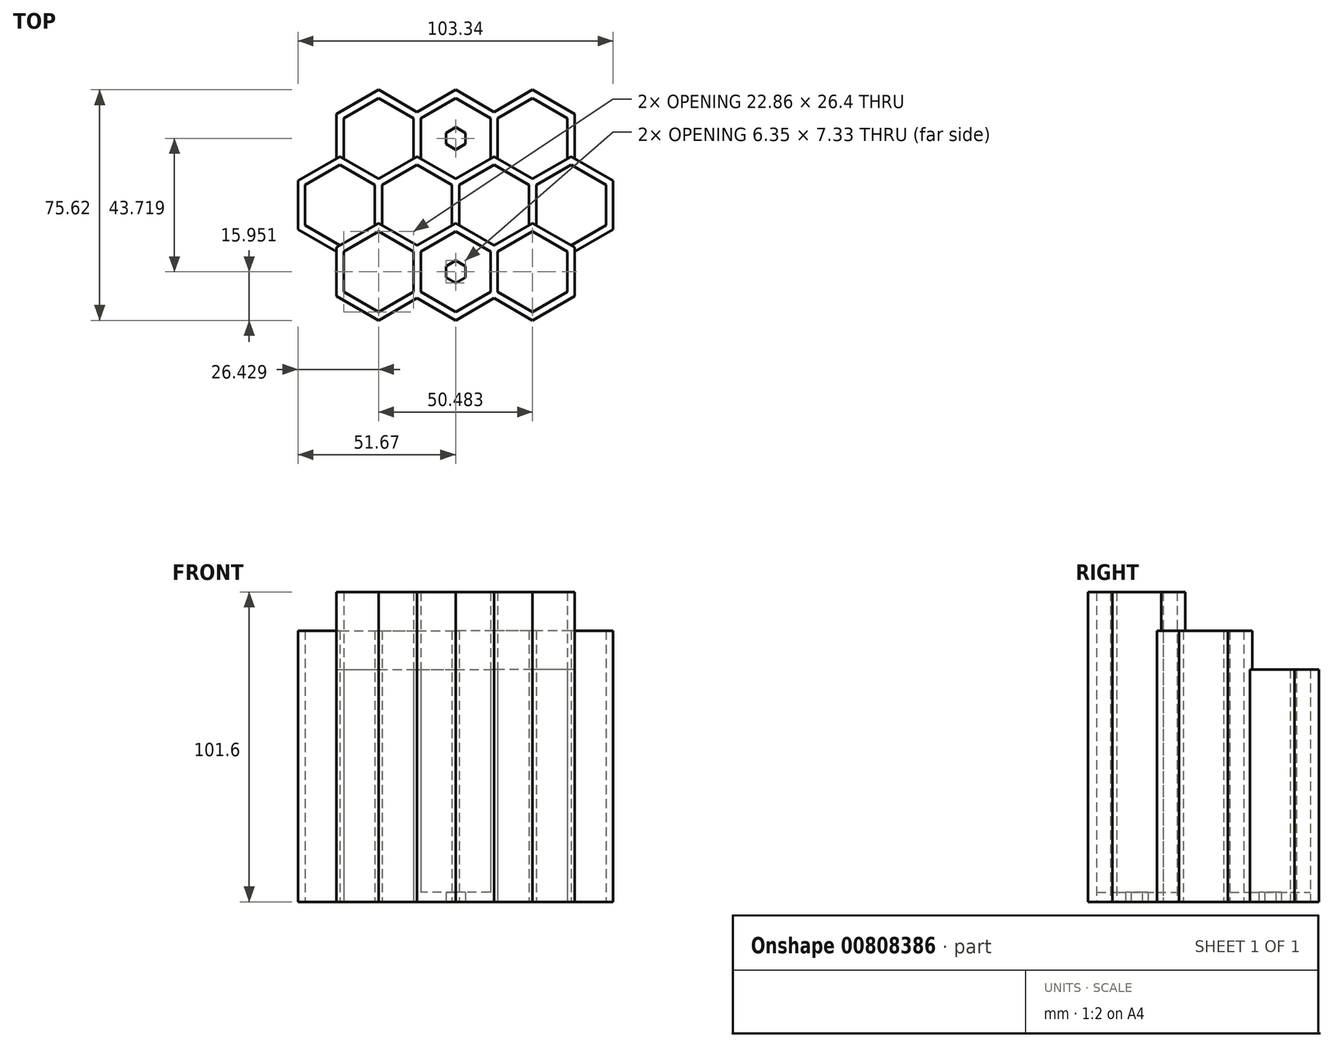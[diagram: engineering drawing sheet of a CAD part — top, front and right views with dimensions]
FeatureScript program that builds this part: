
annotation { "Feature Type Name" : "Feature", "Feature Type Description" : "" }
export const myFeature = defineFeature(function(context is Context, id is Id, definition is map)
    precondition{}
    {
        {
            var Q0;
            Q0=qCreatedBy(makeId("Top.planeOp"),FACE);
            var sketch = newSketch(context, id + "F0", { "sketchPlane" : qUnion([Q0])});
            skCircle(sketch, "E0.cCircle", {"center": v(-12.62, 0) * mm, "radius": 11.43 * mm, "construction": true});
            skLineSegment(sketch, "E0.0", {"start": v(-24.05, -6.6) * mm, "end": v(-24.05, 6.6) * mm});
            skLineSegment(sketch, "E0.1", {"start": v(-24.05, 6.6) * mm, "end": v(-12.62, 13.2) * mm});
            skLineSegment(sketch, "E0.2", {"start": v(-12.62, 13.2) * mm, "end": v(-1.2, 6.6) * mm});
            skLineSegment(sketch, "E0.3", {"start": v(-1.2, 6.6) * mm, "end": v(-1.2, -6.6) * mm});
            skLineSegment(sketch, "E0.4", {"start": v(-1.2, -6.6) * mm, "end": v(-12.62, -13.2) * mm});
            skLineSegment(sketch, "E0.5", {"start": v(-12.62, -13.2) * mm, "end": v(-24.05, -6.6) * mm});
            skPoint(sketch, "E0.0.midPoint", {"position": v(-24.05, 0) * mm});
            skCircle(sketch, "E1.cCircle", {"center": v(-37.86, 0) * mm, "radius": 11.43 * mm, "construction": true});
            skLineSegment(sketch, "E1.0", {"start": v(-49.3, -6.6) * mm, "end": v(-49.3, 6.6) * mm});
            skLineSegment(sketch, "E1.1", {"start": v(-49.3, 6.6) * mm, "end": v(-37.86, 13.2) * mm});
            skLineSegment(sketch, "E1.2", {"start": v(-37.86, 13.2) * mm, "end": v(-26.43, 6.6) * mm});
            skLineSegment(sketch, "E1.3", {"start": v(-26.43, 6.6) * mm, "end": v(-26.43, -6.6) * mm});
            skLineSegment(sketch, "E1.4", {"start": v(-26.43, -6.6) * mm, "end": v(-37.86, -13.2) * mm});
            skLineSegment(sketch, "E1.5", {"start": v(-37.86, -13.2) * mm, "end": v(-49.3, -6.6) * mm});
            skPoint(sketch, "E1.0.midPoint", {"position": v(-49.3, 0) * mm});
            skLineSegment(sketch, "E2.0", {"start": v(-37.86, 15.95) * mm, "end": v(-25.24, 8.66) * mm});
            skLineSegment(sketch, "E2.1", {"start": v(-51.67, 7.97) * mm, "end": v(-37.86, 15.95) * mm});
            skLineSegment(sketch, "E2.2", {"start": v(-51.67, -7.97) * mm, "end": v(-51.67, 7.97) * mm});
            skLineSegment(sketch, "E2.3", {"start": v(-39.05, -15.26) * mm, "end": v(-51.67, -7.97) * mm});
            skLineSegment(sketch, "E3.0", {"start": v(-12.62, 15.95) * mm, "end": v(0, 8.66) * mm});
            skLineSegment(sketch, "E3.1", {"start": v(-25.24, 8.66) * mm, "end": v(-12.62, 15.95) * mm});
            skPoint(sketch, "E4.MirrorP", {"position": v(24.05, 0) * mm});
            skLineSegment(sketch, "E5.MirrorCS", {"start": v(25.24, 8.66) * mm, "end": v(12.62, 15.95) * mm});
            skLineSegment(sketch, "E6.MirrorCS", {"start": v(39.05, -15.26) * mm, "end": v(51.67, -7.97) * mm});
            skLineSegment(sketch, "E7.MirrorCS", {"start": v(37.86, -13.2) * mm, "end": v(49.3, -6.6) * mm});
            skLineSegment(sketch, "E8.MirrorCS", {"start": v(37.86, 15.95) * mm, "end": v(25.24, 8.66) * mm});
            skLineSegment(sketch, "E9.MirrorCS", {"start": v(51.67, 7.97) * mm, "end": v(37.86, 15.95) * mm});
            skLineSegment(sketch, "E10.MirrorCS", {"start": v(24.05, 6.6) * mm, "end": v(12.62, 13.2) * mm});
            skLineSegment(sketch, "E11.MirrorCS", {"start": v(12.62, 13.2) * mm, "end": v(1.2, 6.6) * mm});
            skLineSegment(sketch, "E12.MirrorCS", {"start": v(1.2, 6.6) * mm, "end": v(1.2, -6.6) * mm});
            skLineSegment(sketch, "E13.MirrorCS", {"start": v(1.2, -6.6) * mm, "end": v(12.62, -13.2) * mm});
            skLineSegment(sketch, "E14.MirrorCS", {"start": v(12.62, -13.2) * mm, "end": v(24.05, -6.6) * mm});
            skCircle(sketch, "E15.MirrorC", {"center": v(37.86, 0) * mm, "radius": 11.43 * mm, "construction": true});
            skLineSegment(sketch, "E16.MirrorCS", {"start": v(24.05, -6.6) * mm, "end": v(24.05, 6.6) * mm});
            skPoint(sketch, "E17.MirrorP", {"position": v(49.3, 0) * mm});
            skCircle(sketch, "E18.MirrorC", {"center": v(12.62, 0) * mm, "radius": 11.43 * mm, "construction": true});
            skLineSegment(sketch, "E19.MirrorCS", {"start": v(51.67, -7.97) * mm, "end": v(51.67, 7.97) * mm});
            skLineSegment(sketch, "E20.MirrorCS", {"start": v(12.62, 15.95) * mm, "end": v(0, 8.66) * mm});
            skLineSegment(sketch, "E21.MirrorCS", {"start": v(26.43, -6.6) * mm, "end": v(37.86, -13.2) * mm});
            skLineSegment(sketch, "E22.MirrorCS", {"start": v(26.43, 6.6) * mm, "end": v(26.43, -6.6) * mm});
            skLineSegment(sketch, "E23.MirrorCS", {"start": v(37.86, 13.2) * mm, "end": v(26.43, 6.6) * mm});
            skLineSegment(sketch, "E24.MirrorCS", {"start": v(49.3, -6.6) * mm, "end": v(49.3, 6.6) * mm});
            skLineSegment(sketch, "E25.MirrorCS", {"start": v(49.3, 6.6) * mm, "end": v(37.86, 13.2) * mm});
            skLineSegment(sketch, "E26", {"start": v(-39.05, -15.26) * mm, "end": v(-37.86, -13.2) * mm});
            skLineSegment(sketch, "E27", {"start": v(-26.43, -6.6) * mm, "end": v(-24.05, -6.6) * mm});
            skLineSegment(sketch, "E28", {"start": v(-1.2, -6.6) * mm, "end": v(1.2, -6.6) * mm});
            skLineSegment(sketch, "E29", {"start": v(24.05, -6.6) * mm, "end": v(26.43, -6.6) * mm});
            skLineSegment(sketch, "E30", {"start": v(37.86, -13.2) * mm, "end": v(39.05, -15.26) * mm});
            skSolve(sketch);
        }
        {
            var Q0;
            Q0=qCreatedBy(makeId("Top.planeOp"),FACE);
            var sketch = newSketch(context, id + "F1", { "sketchPlane" : qUnion([Q0])});
            skCircle(sketch, "E31.cCircle", {"center": v(0, -21.86) * mm, "radius": 11.43 * mm, "construction": true});
            skLineSegment(sketch, "E31.0", {"start": v(-11.43, -28.46) * mm, "end": v(-11.43, -15.26) * mm});
            skLineSegment(sketch, "E31.1", {"start": v(-11.43, -15.26) * mm, "end": v(0, -8.66) * mm});
            skLineSegment(sketch, "E31.2", {"start": v(0, -8.66) * mm, "end": v(11.43, -15.26) * mm});
            skLineSegment(sketch, "E31.3", {"start": v(11.43, -15.26) * mm, "end": v(11.43, -28.46) * mm});
            skLineSegment(sketch, "E31.4", {"start": v(11.43, -28.46) * mm, "end": v(0, -35.06) * mm});
            skLineSegment(sketch, "E31.5", {"start": v(0, -35.06) * mm, "end": v(-11.43, -28.46) * mm});
            skPoint(sketch, "E31.0.midPoint", {"position": v(-11.43, -21.86) * mm});
            skLineSegment(sketch, "E32.0", {"start": v(-12.62, -13.2) * mm, "end": v(0, -5.91) * mm});
            skLineSegment(sketch, "E33.0", {"start": v(0, -5.91) * mm, "end": v(12.62, -13.2) * mm});
            skCircle(sketch, "E34.cCircle", {"center": v(-25.24, -21.86) * mm, "radius": 11.43 * mm, "construction": true});
            skLineSegment(sketch, "E34.0", {"start": v(-36.67, -28.46) * mm, "end": v(-36.67, -15.26) * mm});
            skLineSegment(sketch, "E34.1", {"start": v(-36.67, -15.26) * mm, "end": v(-25.24, -8.66) * mm});
            skLineSegment(sketch, "E34.2", {"start": v(-25.24, -8.66) * mm, "end": v(-13.81, -15.26) * mm});
            skLineSegment(sketch, "E34.3", {"start": v(-13.81, -15.26) * mm, "end": v(-13.81, -28.46) * mm});
            skLineSegment(sketch, "E34.4", {"start": v(-13.81, -28.46) * mm, "end": v(-25.24, -35.06) * mm});
            skLineSegment(sketch, "E34.5", {"start": v(-25.24, -35.06) * mm, "end": v(-36.67, -28.46) * mm});
            skPoint(sketch, "E34.0.midPoint", {"position": v(-36.67, -21.86) * mm});
            skLineSegment(sketch, "E35.0", {"start": v(-25.24, -5.91) * mm, "end": v(-12.62, -13.2) * mm});
            skLineSegment(sketch, "E35.1", {"start": v(-12.62, -30.52) * mm, "end": v(-25.24, -37.8) * mm});
            skLineSegment(sketch, "E35.2", {"start": v(-25.24, -37.8) * mm, "end": v(-39.05, -29.83) * mm});
            skLineSegment(sketch, "E35.3", {"start": v(-39.05, -29.83) * mm, "end": v(-39.05, -13.89) * mm});
            skLineSegment(sketch, "E35.4", {"start": v(-39.05, -13.89) * mm, "end": v(-25.24, -5.91) * mm});
            skLineSegment(sketch, "E36.0", {"start": v(0, -37.8) * mm, "end": v(-12.62, -30.52) * mm});
            skLineSegment(sketch, "E36.1", {"start": v(12.62, -30.52) * mm, "end": v(0, -37.8) * mm});
            skLineSegment(sketch, "E37.MirrorCS", {"start": v(13.81, -15.26) * mm, "end": v(13.81, -28.46) * mm});
            skLineSegment(sketch, "E38.MirrorCS", {"start": v(25.24, -8.66) * mm, "end": v(13.81, -15.26) * mm});
            skLineSegment(sketch, "E39.MirrorCS", {"start": v(36.67, -15.26) * mm, "end": v(25.24, -8.66) * mm});
            skLineSegment(sketch, "E40.MirrorCS", {"start": v(36.67, -28.46) * mm, "end": v(36.67, -15.26) * mm});
            skLineSegment(sketch, "E41.MirrorCS", {"start": v(25.24, -35.06) * mm, "end": v(36.67, -28.46) * mm});
            skLineSegment(sketch, "E42.MirrorCS", {"start": v(13.81, -28.46) * mm, "end": v(25.24, -35.06) * mm});
            skLineSegment(sketch, "E43.MirrorCS", {"start": v(12.62, -30.52) * mm, "end": v(25.24, -37.8) * mm});
            skLineSegment(sketch, "E44.MirrorCS", {"start": v(25.24, -37.8) * mm, "end": v(39.05, -29.83) * mm});
            skLineSegment(sketch, "E45.MirrorCS", {"start": v(39.05, -29.83) * mm, "end": v(39.05, -13.89) * mm});
            skLineSegment(sketch, "E46.MirrorCS", {"start": v(39.05, -13.89) * mm, "end": v(25.24, -5.91) * mm});
            skLineSegment(sketch, "E47.MirrorCS", {"start": v(25.24, -5.91) * mm, "end": v(12.62, -13.2) * mm});
            skSolve(sketch);
        }
        {
            var Q0;
            Q0=qCreatedBy(makeId("Top.planeOp"),FACE);
            var sketch = newSketch(context, id + "F2", { "sketchPlane" : qUnion([Q0])});
            skCircle(sketch, "E48.cCircle", {"center": v(0, 21.86) * mm, "radius": 11.43 * mm, "construction": true});
            skLineSegment(sketch, "E48.0", {"start": v(-11.43, 15.26) * mm, "end": v(-11.43, 28.46) * mm});
            skLineSegment(sketch, "E48.1", {"start": v(-11.43, 28.46) * mm, "end": v(0, 35.06) * mm});
            skLineSegment(sketch, "E48.2", {"start": v(0, 35.06) * mm, "end": v(11.43, 28.46) * mm});
            skLineSegment(sketch, "E48.3", {"start": v(11.43, 28.46) * mm, "end": v(11.43, 15.26) * mm});
            skLineSegment(sketch, "E48.4", {"start": v(11.43, 15.26) * mm, "end": v(0, 8.66) * mm});
            skLineSegment(sketch, "E48.5", {"start": v(0, 8.66) * mm, "end": v(-11.43, 15.26) * mm});
            skPoint(sketch, "E48.0.midPoint", {"position": v(-11.43, 21.86) * mm});
            skCircle(sketch, "E49.cCircle", {"center": v(-25.24, 21.86) * mm, "radius": 11.43 * mm, "construction": true});
            skLineSegment(sketch, "E49.0", {"start": v(-36.67, 15.26) * mm, "end": v(-36.67, 28.46) * mm});
            skLineSegment(sketch, "E49.1", {"start": v(-36.67, 28.46) * mm, "end": v(-25.24, 35.06) * mm});
            skLineSegment(sketch, "E49.2", {"start": v(-25.24, 35.06) * mm, "end": v(-13.81, 28.46) * mm});
            skLineSegment(sketch, "E49.3", {"start": v(-13.81, 28.46) * mm, "end": v(-13.81, 15.26) * mm});
            skLineSegment(sketch, "E49.4", {"start": v(-13.81, 15.26) * mm, "end": v(-25.24, 8.66) * mm});
            skLineSegment(sketch, "E49.5", {"start": v(-25.24, 8.66) * mm, "end": v(-36.67, 15.26) * mm});
            skPoint(sketch, "E49.0.midPoint", {"position": v(-36.67, 21.86) * mm});
            skLineSegment(sketch, "E50.0", {"start": v(-25.24, 37.8) * mm, "end": v(-12.62, 30.52) * mm});
            skLineSegment(sketch, "E50.1", {"start": v(-39.05, 29.83) * mm, "end": v(-25.24, 37.8) * mm});
            skLineSegment(sketch, "E50.2", {"start": v(-39.05, 15.26) * mm, "end": v(-39.05, 29.83) * mm});
            skLineSegment(sketch, "E51.0", {"start": v(0, 37.8) * mm, "end": v(12.62, 30.52) * mm});
            skLineSegment(sketch, "E51.1", {"start": v(-12.62, 30.52) * mm, "end": v(0, 37.8) * mm});
            skPoint(sketch, "E52.MirrorP", {"position": v(36.67, 21.86) * mm});
            skCircle(sketch, "E53.MirrorC", {"center": v(25.24, 21.86) * mm, "radius": 11.43 * mm, "construction": true});
            skLineSegment(sketch, "E54.MirrorCS", {"start": v(25.24, 8.66) * mm, "end": v(36.67, 15.26) * mm});
            skLineSegment(sketch, "E55.MirrorCS", {"start": v(36.67, 15.26) * mm, "end": v(36.67, 28.46) * mm});
            skLineSegment(sketch, "E56.MirrorCS", {"start": v(36.67, 28.46) * mm, "end": v(25.24, 35.06) * mm});
            skLineSegment(sketch, "E57.MirrorCS", {"start": v(25.24, 35.06) * mm, "end": v(13.81, 28.46) * mm});
            skLineSegment(sketch, "E58.MirrorCS", {"start": v(13.81, 28.46) * mm, "end": v(13.81, 15.26) * mm});
            skLineSegment(sketch, "E59.MirrorCS", {"start": v(13.81, 15.26) * mm, "end": v(25.24, 8.66) * mm});
            skLineSegment(sketch, "E60.MirrorCS", {"start": v(39.05, 15.26) * mm, "end": v(39.05, 29.83) * mm});
            skPoint(sketch, "E61.MirrorP", {"position": v(11.43, 21.86) * mm});
            skLineSegment(sketch, "E62.MirrorCS", {"start": v(39.05, 29.83) * mm, "end": v(25.24, 37.8) * mm});
            skLineSegment(sketch, "E63.MirrorCS", {"start": v(25.24, 37.8) * mm, "end": v(12.62, 30.52) * mm});
            skLineSegment(sketch, "E64", {"start": v(-39.05, 15.26) * mm, "end": v(-36.67, 15.26) * mm});
            skLineSegment(sketch, "E65", {"start": v(-13.81, 15.26) * mm, "end": v(-11.43, 15.26) * mm});
            skLineSegment(sketch, "E66", {"start": v(11.43, 15.26) * mm, "end": v(13.81, 15.26) * mm});
            skLineSegment(sketch, "E67", {"start": v(36.67, 15.26) * mm, "end": v(39.05, 15.26) * mm});
            skSolve(sketch);
        }
        {
            var Q0;
            Q0 = qSketchRegion(id + "F1", true);
            extrude(context, id + "F3", {"entities" : qUnion([Q0]), "depth" : 101.6 * mm, "offsetDistance" : 25.4 * mm});
        }
        {
            var Q0;
            Q0=makeQuery(id+"F0.imprint","IMPRINT",FACE,{"disambiguationData":[TD([[makeQuery(id+"F0.imprint","IMPRINT",EDGE,{"derivedFrom":sQuery(id+"F0.wireOp",EDGE,"E0.0")}),1.0]])]});
            extrude(context, id + "F4", {"entities" : qUnion([Q0]), "operationType" : NewBodyOperationType.ADD, "depth" : 88.9 * mm, "offsetDistance" : 25.4 * mm});
        }
        {
            var Q0;
            Q0=makeQuery(id+"F2.imprint","IMPRINT",FACE,{"disambiguationData":[TD([[makeQuery(id+"F2.imprint","IMPRINT",EDGE,{"derivedFrom":sQuery(id+"F2.wireOp",EDGE,"E48.0")}),1.0]])]});
            extrude(context, id + "F5", {"entities" : qUnion([Q0]), "operationType" : NewBodyOperationType.ADD, "depth" : 76.2 * mm, "offsetDistance" : 25.4 * mm});
        }
        {
            var Q0;
            Q0=qCreatedBy(makeId("Top.planeOp"),FACE);
            var sketch = newSketch(context, id + "F6", { "sketchPlane" : qUnion([Q0])});
            skCircle(sketch, "E68.cCircle", {"center": v(-12.62, 0) * mm, "radius": 11.43 * mm, "construction": true});
            skLineSegment(sketch, "E68.0", {"start": v(-24.05, -6.6) * mm, "end": v(-24.05, 6.6) * mm});
            skLineSegment(sketch, "E68.1", {"start": v(-24.05, 6.6) * mm, "end": v(-12.62, 13.2) * mm});
            skLineSegment(sketch, "E68.2", {"start": v(-12.62, 13.2) * mm, "end": v(-1.2, 6.6) * mm});
            skLineSegment(sketch, "E68.3", {"start": v(-1.2, 6.6) * mm, "end": v(-1.2, -6.6) * mm});
            skLineSegment(sketch, "E68.4", {"start": v(-1.2, -6.6) * mm, "end": v(-12.62, -13.2) * mm});
            skLineSegment(sketch, "E68.5", {"start": v(-12.62, -13.2) * mm, "end": v(-24.05, -6.6) * mm});
            skPoint(sketch, "E68.0.midPoint", {"position": v(-24.05, 0) * mm});
            skLineSegment(sketch, "E69.0", {"start": v(-49.3, -6.6) * mm, "end": v(-49.3, 6.6) * mm});
            skLineSegment(sketch, "E69.1", {"start": v(-49.3, 6.6) * mm, "end": v(-37.86, 13.2) * mm});
            skLineSegment(sketch, "E69.2", {"start": v(-37.86, 13.2) * mm, "end": v(-26.43, 6.6) * mm});
            skLineSegment(sketch, "E69.3", {"start": v(-26.43, 6.6) * mm, "end": v(-26.43, -6.6) * mm});
            skLineSegment(sketch, "E69.4", {"start": v(-26.43, -6.6) * mm, "end": v(-37.86, -13.2) * mm});
            skLineSegment(sketch, "E69.5", {"start": v(-37.86, -13.2) * mm, "end": v(-49.3, -6.6) * mm});
            skPoint(sketch, "E69.0.midPoint", {"position": v(-49.3, 0) * mm});
            skCircle(sketch, "E70.cCircle", {"center": v(-25.24, 21.86) * mm, "radius": 11.43 * mm, "construction": true});
            skLineSegment(sketch, "E70.0", {"start": v(-36.67, 15.26) * mm, "end": v(-36.67, 28.46) * mm});
            skLineSegment(sketch, "E70.1", {"start": v(-36.67, 28.46) * mm, "end": v(-25.24, 35.06) * mm});
            skLineSegment(sketch, "E70.2", {"start": v(-25.24, 35.06) * mm, "end": v(-13.81, 28.46) * mm});
            skLineSegment(sketch, "E70.3", {"start": v(-13.81, 28.46) * mm, "end": v(-13.81, 15.26) * mm});
            skLineSegment(sketch, "E70.4", {"start": v(-13.81, 15.26) * mm, "end": v(-25.24, 8.66) * mm});
            skLineSegment(sketch, "E70.5", {"start": v(-25.24, 8.66) * mm, "end": v(-36.67, 15.26) * mm});
            skPoint(sketch, "E70.0.midPoint", {"position": v(-36.67, 21.86) * mm});
            skLineSegment(sketch, "E71.MirrorCS", {"start": v(-13.81, -15.26) * mm, "end": v(-25.24, -8.66) * mm});
            skLineSegment(sketch, "E72.MirrorCS", {"start": v(-25.24, -8.66) * mm, "end": v(-36.67, -15.26) * mm});
            skLineSegment(sketch, "E73.MirrorCS", {"start": v(-36.67, -15.26) * mm, "end": v(-36.67, -28.46) * mm});
            skLineSegment(sketch, "E74.MirrorCS", {"start": v(-36.67, -28.46) * mm, "end": v(-25.24, -35.06) * mm});
            skLineSegment(sketch, "E75.MirrorCS", {"start": v(-25.24, -35.06) * mm, "end": v(-13.81, -28.46) * mm});
            skLineSegment(sketch, "E76.MirrorCS", {"start": v(-13.81, -28.46) * mm, "end": v(-13.81, -15.26) * mm});
            skLineSegment(sketch, "E77.MirrorCS", {"start": v(-1.2, -6.6) * mm, "end": v(-1.2, 6.6) * mm});
            skLineSegment(sketch, "E78.MirrorCS", {"start": v(-49.3, 6.6) * mm, "end": v(-49.3, -6.6) * mm});
            skLineSegment(sketch, "E79.MirrorCS", {"start": v(-26.43, -6.6) * mm, "end": v(-26.43, 6.6) * mm});
            skLineSegment(sketch, "E80.MirrorCS", {"start": v(-24.05, -6.6) * mm, "end": v(-12.62, -13.2) * mm});
            skLineSegment(sketch, "E81.MirrorCS", {"start": v(-36.67, 28.46) * mm, "end": v(-36.67, 15.26) * mm});
            skLineSegment(sketch, "E82.MirrorCS", {"start": v(-24.05, 6.6) * mm, "end": v(-24.05, -6.6) * mm});
            skLineSegment(sketch, "E83.MirrorCS", {"start": v(-37.86, -13.2) * mm, "end": v(-26.43, -6.6) * mm});
            skLineSegment(sketch, "E84.MirrorCS", {"start": v(-1.2, 6.6) * mm, "end": v(-12.62, 13.2) * mm});
            skPoint(sketch, "E85.MirrorP", {"position": v(-13.81, 21.86) * mm});
            skLineSegment(sketch, "E86.MirrorCS", {"start": v(-13.81, 15.26) * mm, "end": v(-13.81, 28.46) * mm});
            skLineSegment(sketch, "E87.MirrorCS", {"start": v(-49.3, -6.6) * mm, "end": v(-37.86, -13.2) * mm});
            skLineSegment(sketch, "E88.MirrorCS", {"start": v(-12.62, 13.2) * mm, "end": v(-24.05, 6.6) * mm});
            skLineSegment(sketch, "E89.MirrorCS", {"start": v(-26.43, 6.6) * mm, "end": v(-37.86, 13.2) * mm});
            skLineSegment(sketch, "E90.MirrorCS", {"start": v(-13.81, -15.26) * mm, "end": v(-13.81, -28.46) * mm});
            skLineSegment(sketch, "E91.MirrorCS", {"start": v(-37.86, 13.2) * mm, "end": v(-49.3, 6.6) * mm});
            skLineSegment(sketch, "E92.MirrorCS", {"start": v(-13.81, 28.46) * mm, "end": v(-25.24, 35.06) * mm});
            skLineSegment(sketch, "E93.MirrorCS", {"start": v(-25.24, 8.66) * mm, "end": v(-13.81, 15.26) * mm});
            skLineSegment(sketch, "E94.MirrorCS", {"start": v(-36.67, -28.46) * mm, "end": v(-36.67, -15.26) * mm});
            skLineSegment(sketch, "E95.MirrorCS", {"start": v(-13.81, -28.46) * mm, "end": v(-25.24, -35.06) * mm});
            skLineSegment(sketch, "E96.MirrorCS", {"start": v(-36.67, -15.26) * mm, "end": v(-25.24, -8.66) * mm});
            skPoint(sketch, "E97.MirrorP", {"position": v(-1.2, 0) * mm});
            skLineSegment(sketch, "E98.MirrorCS", {"start": v(-36.67, 15.26) * mm, "end": v(-25.24, 8.66) * mm});
            skLineSegment(sketch, "E99.MirrorCS", {"start": v(-25.24, -35.06) * mm, "end": v(-36.67, -28.46) * mm});
            skPoint(sketch, "E100.MirrorP", {"position": v(-26.43, 0) * mm});
            skLineSegment(sketch, "E101.MirrorCS", {"start": v(-25.24, -8.66) * mm, "end": v(-13.81, -15.26) * mm});
            skLineSegment(sketch, "E102.MirrorCS", {"start": v(-12.62, -13.2) * mm, "end": v(-1.2, -6.6) * mm});
            skLineSegment(sketch, "E103.MirrorCS", {"start": v(-25.24, 35.06) * mm, "end": v(-36.67, 28.46) * mm});
            skLineSegment(sketch, "E104.MirrorCS", {"start": v(24.05, 6.6) * mm, "end": v(24.05, -6.6) * mm});
            skLineSegment(sketch, "E105.MirrorCS", {"start": v(13.81, 15.26) * mm, "end": v(13.81, 28.46) * mm});
            skLineSegment(sketch, "E106.MirrorCS", {"start": v(26.43, -6.6) * mm, "end": v(26.43, 6.6) * mm});
            skLineSegment(sketch, "E107.MirrorCS", {"start": v(25.24, 8.66) * mm, "end": v(36.67, 15.26) * mm});
            skLineSegment(sketch, "E108.MirrorCS", {"start": v(12.62, -13.2) * mm, "end": v(1.2, -6.6) * mm});
            skLineSegment(sketch, "E109.MirrorCS", {"start": v(25.24, 8.66) * mm, "end": v(13.81, 15.26) * mm});
            skLineSegment(sketch, "E110.MirrorCS", {"start": v(49.3, 6.6) * mm, "end": v(49.3, -6.6) * mm});
            skLineSegment(sketch, "E111.MirrorCS", {"start": v(24.05, -6.6) * mm, "end": v(12.62, -13.2) * mm});
            skLineSegment(sketch, "E112.MirrorCS", {"start": v(25.24, 35.06) * mm, "end": v(36.67, 28.46) * mm});
            skLineSegment(sketch, "E113.MirrorCS", {"start": v(12.62, 13.2) * mm, "end": v(24.05, 6.6) * mm});
            skLineSegment(sketch, "E114.MirrorCS", {"start": v(26.43, 6.6) * mm, "end": v(37.86, 13.2) * mm});
            skLineSegment(sketch, "E115.MirrorCS", {"start": v(36.67, 28.46) * mm, "end": v(36.67, 15.26) * mm});
            skLineSegment(sketch, "E116.MirrorCS", {"start": v(37.86, -13.2) * mm, "end": v(26.43, -6.6) * mm});
            skLineSegment(sketch, "E117.MirrorCS", {"start": v(36.67, 28.46) * mm, "end": v(25.24, 35.06) * mm});
            skLineSegment(sketch, "E118.MirrorCS", {"start": v(37.86, 13.2) * mm, "end": v(26.43, 6.6) * mm});
            skLineSegment(sketch, "E119.MirrorCS", {"start": v(26.43, 6.6) * mm, "end": v(26.43, -6.6) * mm});
            skLineSegment(sketch, "E120.MirrorCS", {"start": v(26.43, -6.6) * mm, "end": v(37.86, -13.2) * mm});
            skLineSegment(sketch, "E121.MirrorCS", {"start": v(49.3, -6.6) * mm, "end": v(49.3, 6.6) * mm});
            skLineSegment(sketch, "E122.MirrorCS", {"start": v(1.2, -6.6) * mm, "end": v(1.2, 6.6) * mm});
            skLineSegment(sketch, "E123.MirrorCS", {"start": v(36.67, -15.26) * mm, "end": v(36.67, -28.46) * mm});
            skLineSegment(sketch, "E124.MirrorCS", {"start": v(36.67, 15.26) * mm, "end": v(25.24, 8.66) * mm});
            skLineSegment(sketch, "E125.MirrorCS", {"start": v(1.2, -6.6) * mm, "end": v(12.62, -13.2) * mm});
            skLineSegment(sketch, "E126.MirrorCS", {"start": v(24.05, 6.6) * mm, "end": v(12.62, 13.2) * mm});
            skLineSegment(sketch, "E127.MirrorCS", {"start": v(12.62, -13.2) * mm, "end": v(24.05, -6.6) * mm});
            skLineSegment(sketch, "E128.MirrorCS", {"start": v(13.81, -15.26) * mm, "end": v(13.81, -28.46) * mm});
            skLineSegment(sketch, "E129.MirrorCS", {"start": v(13.81, 15.26) * mm, "end": v(25.24, 8.66) * mm});
            skLineSegment(sketch, "E130.MirrorCS", {"start": v(24.05, -6.6) * mm, "end": v(24.05, 6.6) * mm});
            skLineSegment(sketch, "E131.MirrorCS", {"start": v(36.67, 15.26) * mm, "end": v(36.67, 28.46) * mm});
            skLineSegment(sketch, "E132.MirrorCS", {"start": v(13.81, 28.46) * mm, "end": v(13.81, 15.26) * mm});
            skLineSegment(sketch, "E133.MirrorCS", {"start": v(25.24, -8.66) * mm, "end": v(13.81, -15.26) * mm});
            skLineSegment(sketch, "E134.MirrorCS", {"start": v(36.67, -15.26) * mm, "end": v(25.24, -8.66) * mm});
            skLineSegment(sketch, "E135.MirrorCS", {"start": v(37.86, 13.2) * mm, "end": v(49.3, 6.6) * mm});
            skCircle(sketch, "E136.MirrorC", {"center": v(25.24, 21.86) * mm, "radius": 11.43 * mm, "construction": true});
            skCircle(sketch, "E137.MirrorC", {"center": v(12.62, 0) * mm, "radius": 11.43 * mm, "construction": true});
            skLineSegment(sketch, "E138.MirrorCS", {"start": v(25.24, 35.06) * mm, "end": v(13.81, 28.46) * mm});
            skLineSegment(sketch, "E139.MirrorCS", {"start": v(49.3, -6.6) * mm, "end": v(37.86, -13.2) * mm});
            skLineSegment(sketch, "E140.MirrorCS", {"start": v(13.81, -15.26) * mm, "end": v(25.24, -8.66) * mm});
            skLineSegment(sketch, "E141.MirrorCS", {"start": v(36.67, -28.46) * mm, "end": v(36.67, -15.26) * mm});
            skCircle(sketch, "E142.MirrorC", {"center": v(37.86, 0) * mm, "radius": 11.43 * mm, "construction": true});
            skLineSegment(sketch, "E143.MirrorCS", {"start": v(13.81, -28.46) * mm, "end": v(13.81, -15.26) * mm});
            skLineSegment(sketch, "E144.MirrorCS", {"start": v(1.2, 6.6) * mm, "end": v(1.2, -6.6) * mm});
            skLineSegment(sketch, "E145.MirrorCS", {"start": v(25.24, -35.06) * mm, "end": v(36.67, -28.46) * mm});
            skLineSegment(sketch, "E146.MirrorCS", {"start": v(25.24, -35.06) * mm, "end": v(13.81, -28.46) * mm});
            skLineSegment(sketch, "E147.MirrorCS", {"start": v(1.2, 6.6) * mm, "end": v(12.62, 13.2) * mm});
            skLineSegment(sketch, "E148.MirrorCS", {"start": v(49.3, 6.6) * mm, "end": v(37.86, 13.2) * mm});
            skPoint(sketch, "E149.MirrorP", {"position": v(13.81, 21.86) * mm});
            skPoint(sketch, "E150.MirrorP", {"position": v(26.43, 0) * mm});
            skPoint(sketch, "E151.MirrorP", {"position": v(36.67, 21.86) * mm});
            skLineSegment(sketch, "E152.MirrorCS", {"start": v(13.81, 28.46) * mm, "end": v(25.24, 35.06) * mm});
            skPoint(sketch, "E153.MirrorP", {"position": v(24.05, 0) * mm});
            skPoint(sketch, "E154.MirrorP", {"position": v(49.3, 0) * mm});
            skLineSegment(sketch, "E155.MirrorCS", {"start": v(12.62, 13.2) * mm, "end": v(1.2, 6.6) * mm});
            skLineSegment(sketch, "E156.MirrorCS", {"start": v(25.24, -8.66) * mm, "end": v(36.67, -15.26) * mm});
            skPoint(sketch, "E157.MirrorP", {"position": v(1.2, 0) * mm});
            skLineSegment(sketch, "E158.MirrorCS", {"start": v(36.67, -28.46) * mm, "end": v(25.24, -35.06) * mm});
            skLineSegment(sketch, "E159.MirrorCS", {"start": v(13.81, -28.46) * mm, "end": v(25.24, -35.06) * mm});
            skLineSegment(sketch, "E160.MirrorCS", {"start": v(37.86, -13.2) * mm, "end": v(49.3, -6.6) * mm});
            skCircle(sketch, "E161.cCircle", {"center": v(0, 21.86) * mm, "radius": 11.43 * mm, "construction": true});
            skLineSegment(sketch, "E161.0", {"start": v(-11.43, 15.26) * mm, "end": v(-11.43, 28.46) * mm});
            skLineSegment(sketch, "E161.1", {"start": v(-11.43, 28.46) * mm, "end": v(0, 35.06) * mm});
            skLineSegment(sketch, "E161.2", {"start": v(0, 35.06) * mm, "end": v(11.43, 28.46) * mm});
            skLineSegment(sketch, "E161.3", {"start": v(11.43, 28.46) * mm, "end": v(11.43, 15.26) * mm});
            skLineSegment(sketch, "E161.4", {"start": v(11.43, 15.26) * mm, "end": v(0, 8.66) * mm});
            skLineSegment(sketch, "E161.5", {"start": v(0, 8.66) * mm, "end": v(-11.43, 15.26) * mm});
            skPoint(sketch, "E161.0.midPoint", {"position": v(-11.43, 21.86) * mm});
            skCircle(sketch, "E162.cCircle", {"center": v(0, -21.86) * mm, "radius": 11.43 * mm, "construction": true});
            skLineSegment(sketch, "E162.0", {"start": v(-11.43, -28.46) * mm, "end": v(-11.43, -15.26) * mm});
            skLineSegment(sketch, "E162.1", {"start": v(-11.43, -15.26) * mm, "end": v(0, -8.66) * mm});
            skLineSegment(sketch, "E162.2", {"start": v(0, -8.66) * mm, "end": v(11.43, -15.26) * mm});
            skLineSegment(sketch, "E162.3", {"start": v(11.43, -15.26) * mm, "end": v(11.43, -28.46) * mm});
            skLineSegment(sketch, "E162.4", {"start": v(11.43, -28.46) * mm, "end": v(0, -35.06) * mm});
            skLineSegment(sketch, "E162.5", {"start": v(0, -35.06) * mm, "end": v(-11.43, -28.46) * mm});
            skPoint(sketch, "E162.0.midPoint", {"position": v(-11.43, -21.86) * mm});
            skLineSegment(sketch, "E163.0", {"start": v(25.24, -18.2) * mm, "end": v(22.07, -20.03) * mm});
            skLineSegment(sketch, "E163.1", {"start": v(22.07, -23.7) * mm, "end": v(25.24, -25.53) * mm});
            skLineSegment(sketch, "E163.2", {"start": v(25.24, -25.53) * mm, "end": v(28.42, -23.7) * mm});
            skLineSegment(sketch, "E163.3", {"start": v(22.07, -20.03) * mm, "end": v(22.07, -23.7) * mm});
            skLineSegment(sketch, "E163.4", {"start": v(28.42, -23.7) * mm, "end": v(28.42, -20.03) * mm});
            skLineSegment(sketch, "E163.5", {"start": v(28.42, -20.03) * mm, "end": v(25.24, -18.2) * mm});
            skLineSegment(sketch, "E164.0", {"start": v(-3.18, -20.03) * mm, "end": v(-3.18, -23.7) * mm});
            skLineSegment(sketch, "E164.1", {"start": v(0, -25.53) * mm, "end": v(3.18, -23.7) * mm});
            skLineSegment(sketch, "E164.2", {"start": v(3.18, -23.7) * mm, "end": v(3.18, -20.03) * mm});
            skLineSegment(sketch, "E164.3", {"start": v(-3.18, -23.7) * mm, "end": v(0, -25.53) * mm});
            skLineSegment(sketch, "E164.4", {"start": v(3.18, -20.03) * mm, "end": v(0, -18.2) * mm});
            skLineSegment(sketch, "E164.5", {"start": v(0, -18.2) * mm, "end": v(-3.18, -20.03) * mm});
            skLineSegment(sketch, "E165.0", {"start": v(-28.42, -20.03) * mm, "end": v(-28.42, -23.7) * mm});
            skLineSegment(sketch, "E165.1", {"start": v(-25.24, -25.53) * mm, "end": v(-22.07, -23.7) * mm});
            skLineSegment(sketch, "E165.2", {"start": v(-22.07, -23.7) * mm, "end": v(-22.07, -20.03) * mm});
            skLineSegment(sketch, "E165.3", {"start": v(-28.42, -23.7) * mm, "end": v(-25.24, -25.53) * mm});
            skLineSegment(sketch, "E165.4", {"start": v(-22.07, -20.03) * mm, "end": v(-25.24, -18.2) * mm});
            skLineSegment(sketch, "E165.5", {"start": v(-25.24, -18.2) * mm, "end": v(-28.42, -20.03) * mm});
            skLineSegment(sketch, "E166.0", {"start": v(-41.04, -1.83) * mm, "end": v(-37.86, -3.67) * mm});
            skLineSegment(sketch, "E166.1", {"start": v(-34.69, -1.83) * mm, "end": v(-34.69, 1.83) * mm});
            skLineSegment(sketch, "E166.2", {"start": v(-34.69, 1.83) * mm, "end": v(-37.86, 3.67) * mm});
            skLineSegment(sketch, "E166.3", {"start": v(-37.86, -3.67) * mm, "end": v(-34.69, -1.83) * mm});
            skLineSegment(sketch, "E166.4", {"start": v(-37.86, 3.67) * mm, "end": v(-41.04, 1.83) * mm});
            skLineSegment(sketch, "E166.5", {"start": v(-41.04, 1.83) * mm, "end": v(-41.04, -1.83) * mm});
            skLineSegment(sketch, "E167.0", {"start": v(-15.8, 1.83) * mm, "end": v(-15.8, -1.83) * mm});
            skLineSegment(sketch, "E167.1", {"start": v(-12.62, -3.67) * mm, "end": v(-9.45, -1.83) * mm});
            skLineSegment(sketch, "E167.2", {"start": v(-9.45, -1.83) * mm, "end": v(-9.45, 1.83) * mm});
            skLineSegment(sketch, "E167.3", {"start": v(-15.8, -1.83) * mm, "end": v(-12.62, -3.67) * mm});
            skLineSegment(sketch, "E167.4", {"start": v(-9.45, 1.83) * mm, "end": v(-12.62, 3.67) * mm});
            skLineSegment(sketch, "E167.5", {"start": v(-12.62, 3.67) * mm, "end": v(-15.8, 1.83) * mm});
            skLineSegment(sketch, "E168.0", {"start": v(9.45, -1.83) * mm, "end": v(12.62, -3.67) * mm});
            skLineSegment(sketch, "E168.1", {"start": v(15.8, -1.83) * mm, "end": v(15.8, 1.83) * mm});
            skLineSegment(sketch, "E168.2", {"start": v(15.8, 1.83) * mm, "end": v(12.62, 3.67) * mm});
            skLineSegment(sketch, "E168.3", {"start": v(12.62, -3.67) * mm, "end": v(15.8, -1.83) * mm});
            skLineSegment(sketch, "E168.4", {"start": v(12.62, 3.67) * mm, "end": v(9.45, 1.83) * mm});
            skLineSegment(sketch, "E168.5", {"start": v(9.45, 1.83) * mm, "end": v(9.45, -1.83) * mm});
            skLineSegment(sketch, "E169.0", {"start": v(37.86, 3.67) * mm, "end": v(34.69, 1.83) * mm});
            skLineSegment(sketch, "E169.1", {"start": v(34.69, -1.83) * mm, "end": v(37.86, -3.67) * mm});
            skLineSegment(sketch, "E169.2", {"start": v(37.86, -3.67) * mm, "end": v(41.04, -1.83) * mm});
            skLineSegment(sketch, "E169.3", {"start": v(34.69, 1.83) * mm, "end": v(34.69, -1.83) * mm});
            skLineSegment(sketch, "E169.4", {"start": v(41.04, -1.83) * mm, "end": v(41.04, 1.83) * mm});
            skLineSegment(sketch, "E169.5", {"start": v(41.04, 1.83) * mm, "end": v(37.86, 3.67) * mm});
            skLineSegment(sketch, "E170.0", {"start": v(-28.42, 20.03) * mm, "end": v(-25.24, 18.2) * mm});
            skLineSegment(sketch, "E170.1", {"start": v(-22.07, 20.03) * mm, "end": v(-22.07, 23.7) * mm});
            skLineSegment(sketch, "E170.2", {"start": v(-22.07, 23.7) * mm, "end": v(-25.24, 25.53) * mm});
            skLineSegment(sketch, "E170.3", {"start": v(-25.24, 18.2) * mm, "end": v(-22.07, 20.03) * mm});
            skLineSegment(sketch, "E170.4", {"start": v(-25.24, 25.53) * mm, "end": v(-28.42, 23.7) * mm});
            skLineSegment(sketch, "E170.5", {"start": v(-28.42, 23.7) * mm, "end": v(-28.42, 20.03) * mm});
            skLineSegment(sketch, "E171.0", {"start": v(-3.17, 23.7) * mm, "end": v(-3.17, 20.03) * mm});
            skLineSegment(sketch, "E171.1", {"start": v(0, 18.2) * mm, "end": v(3.18, 20.03) * mm});
            skLineSegment(sketch, "E171.2", {"start": v(3.18, 20.03) * mm, "end": v(3.18, 23.7) * mm});
            skLineSegment(sketch, "E171.3", {"start": v(-3.18, 20.03) * mm, "end": v(0, 18.2) * mm});
            skLineSegment(sketch, "E171.4", {"start": v(3.18, 23.7) * mm, "end": v(0, 25.53) * mm});
            skLineSegment(sketch, "E171.5", {"start": v(0, 25.53) * mm, "end": v(-3.18, 23.7) * mm});
            skLineSegment(sketch, "E172.0", {"start": v(28.42, 23.7) * mm, "end": v(25.24, 25.53) * mm});
            skLineSegment(sketch, "E172.1", {"start": v(22.07, 23.7) * mm, "end": v(22.07, 20.03) * mm});
            skLineSegment(sketch, "E172.2", {"start": v(22.07, 20.03) * mm, "end": v(25.24, 18.2) * mm});
            skLineSegment(sketch, "E172.3", {"start": v(25.24, 25.53) * mm, "end": v(22.07, 23.7) * mm});
            skLineSegment(sketch, "E172.4", {"start": v(25.24, 18.2) * mm, "end": v(28.42, 20.03) * mm});
            skLineSegment(sketch, "E172.5", {"start": v(28.42, 20.03) * mm, "end": v(28.42, 23.7) * mm});
            skSolve(sketch);
        }
        {
            var Q0;
            Q0=makeQuery(id+"F6.imprint","IMPRINT",FACE,{"disambiguationData":[TD([[makeQuery(id+"F6.imprint","IMPRINT",EDGE,{"derivedFrom":sQuery(id+"F6.wireOp",EDGE,"E78.MirrorCS")}),1.0]])]});
            var Q1;
            Q1=makeQuery(id+"F6.imprint","IMPRINT",FACE,{"disambiguationData":[TD([[makeQuery(id+"F6.imprint","IMPRINT",EDGE,{"derivedFrom":sQuery(id+"F6.wireOp",EDGE,"E77.MirrorCS")}),1.0]])]});
            var Q2;
            Q2=makeQuery(id+"F6.imprint","IMPRINT",FACE,{"disambiguationData":[TD([[makeQuery(id+"F6.imprint","IMPRINT",EDGE,{"derivedFrom":sQuery(id+"F6.wireOp",EDGE,"E90.MirrorCS")}),-1.0]])]});
            var Q3;
            Q3=makeQuery(id+"F6.imprint","IMPRINT",FACE,{"disambiguationData":[TD([[makeQuery(id+"F6.imprint","IMPRINT",EDGE,{"derivedFrom":sQuery(id+"F6.wireOp",EDGE,"E81.MirrorCS")}),1.0]])]});
            var Q4;
            Q4=makeQuery(id+"F6.imprint","IMPRINT",FACE,{"disambiguationData":[TD([[makeQuery(id+"F6.imprint","IMPRINT",EDGE,{"derivedFrom":sQuery(id+"F6.wireOp",EDGE,"E161.0")}),-1.0]])]});
            var Q5;
            Q5=makeQuery(id+"F6.imprint","IMPRINT",FACE,{"disambiguationData":[TD([[makeQuery(id+"F6.imprint","IMPRINT",EDGE,{"derivedFrom":sQuery(id+"F6.wireOp",EDGE,"E117.MirrorCS")}),1.0]])]});
            var Q6;
            Q6=makeQuery(id+"F6.imprint","IMPRINT",FACE,{"disambiguationData":[TD([[makeQuery(id+"F6.imprint","IMPRINT",EDGE,{"derivedFrom":sQuery(id+"F6.wireOp",EDGE,"E125.MirrorCS")}),1.0]])]});
            var Q7;
            Q7=makeQuery(id+"F6.imprint","IMPRINT",FACE,{"disambiguationData":[TD([[makeQuery(id+"F6.imprint","IMPRINT",EDGE,{"derivedFrom":sQuery(id+"F6.wireOp",EDGE,"E118.MirrorCS")}),1.0]])]});
            var Q8;
            Q8=makeQuery(id+"F6.imprint","IMPRINT",FACE,{"disambiguationData":[TD([[makeQuery(id+"F6.imprint","IMPRINT",EDGE,{"derivedFrom":sQuery(id+"F6.wireOp",EDGE,"E140.MirrorCS")}),-1.0]])]});
            var Q9;
            Q9=makeQuery(id+"F6.imprint","IMPRINT",FACE,{"disambiguationData":[TD([[makeQuery(id+"F6.imprint","IMPRINT",EDGE,{"derivedFrom":sQuery(id+"F6.wireOp",EDGE,"E162.0")}),-1.0]])]});
            extrude(context, id + "F7", {"entities" : qUnion([Q0, Q1, Q2, Q3, Q4, Q5, Q6, Q7, Q8, Q9]), "operationType" : NewBodyOperationType.ADD, "depth" : 3.17 * mm, "offsetDistance" : 25.4 * mm});
        }
    });
